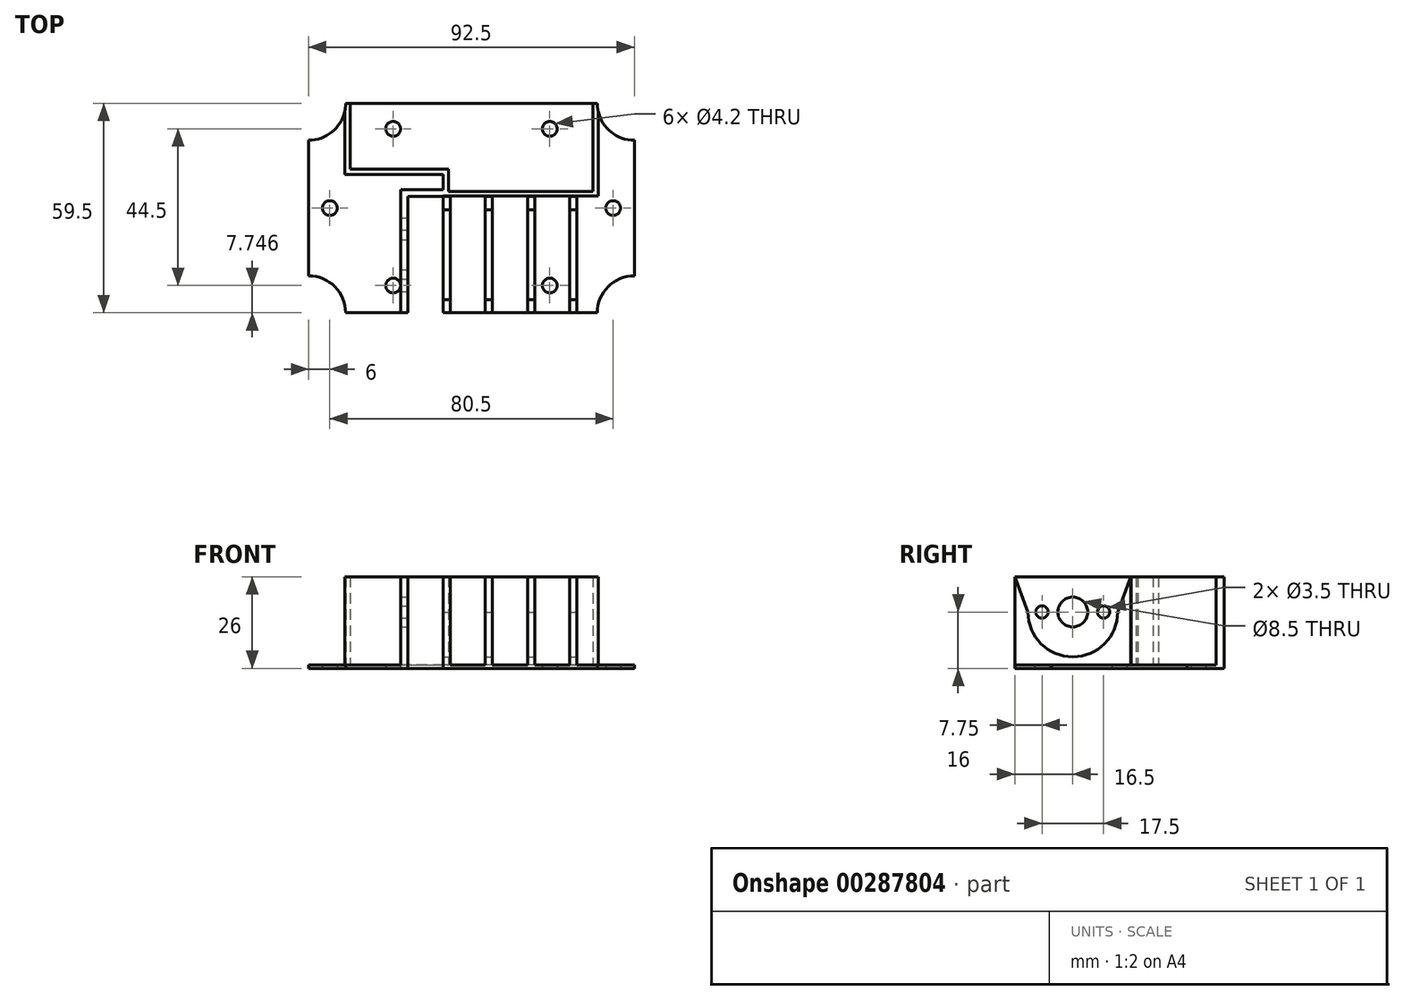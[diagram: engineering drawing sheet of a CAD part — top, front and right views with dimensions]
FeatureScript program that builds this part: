
annotation { "Feature Type Name" : "Feature", "Feature Type Description" : "" }
export const myFeature = defineFeature(function(context is Context, id is Id, definition is map)
    precondition{}
    {
        {
            var Q0;
            Q0=qCreatedBy(makeId("Top.planeOp"),FACE);
            var sketch = newSketch(context, id + "F0", { "sketchPlane" : qUnion([Q0])});
            skLineSegment(sketch, "E0", {"start": v(-40.25, 0) * mm, "end": v(40.25, 0) * mm, "construction": true});
            skLineSegment(sketch, "E1", {"start": v(22.25, 22.5) * mm, "end": v(22.25, -22) * mm, "construction": true});
            skPoint(sketch, "E2", {"position": v(0, 0) * mm});
            skLineSegment(sketch, "E3", {"start": v(22.25, 22.5) * mm, "end": v(-22.25, 22.5) * mm, "construction": true});
            skLineSegment(sketch, "E4", {"start": v(-22.25, 22.5) * mm, "end": v(-22.25, -22) * mm, "construction": true});
            skLineSegment(sketch, "E5", {"start": v(-22.25, -22) * mm, "end": v(22.25, -22) * mm, "construction": true});
            skLineSegment(sketch, "E6", {"start": v(0, 22.5) * mm, "end": v(0, -22) * mm, "construction": true});
            skCircle(sketch, "E7", {"center": v(-22.25, 22.5) * mm, "radius": 2.1 * mm});
            skCircle(sketch, "E8", {"center": v(22.25, 22.5) * mm, "radius": 2.1 * mm});
            skCircle(sketch, "E9", {"center": v(22.25, -22) * mm, "radius": 2.1 * mm});
            skCircle(sketch, "E10", {"center": v(-22.25, -22) * mm, "radius": 2.1 * mm});
            skCircle(sketch, "E11", {"center": v(-40.25, 0) * mm, "radius": 2.1 * mm});
            skCircle(sketch, "E12", {"center": v(40.25, 0) * mm, "radius": 2.1 * mm});
            skLineSegment(sketch, "E13.bottom", {"start": v(46.25, 29.75) * mm, "end": v(-46.25, 29.75) * mm});
            skLineSegment(sketch, "E13.top", {"start": v(46.25, -29.75) * mm, "end": v(-46.25, -29.75) * mm});
            skLineSegment(sketch, "E13.left", {"start": v(46.25, 29.75) * mm, "end": v(46.25, -29.75) * mm});
            skLineSegment(sketch, "E13.right", {"start": v(-46.25, 29.75) * mm, "end": v(-46.25, -29.75) * mm});
            skCircle(sketch, "E14", {"center": v(-46.25, 29.75) * mm, "radius": 10.5 * mm});
            skCircle(sketch, "E15.MirrorC", {"center": v(46.25, 29.75) * mm, "radius": 10.5 * mm});
            skCircle(sketch, "E16.MirrorC", {"center": v(-46.25, -29.75) * mm, "radius": 10.5 * mm});
            skCircle(sketch, "E17.MirrorC", {"center": v(46.25, -29.75) * mm, "radius": 10.5 * mm});
            skSolve(sketch);
        }
        {
            var Q0;
            Q0=makeQuery(id+"F0.imprint","IMPRINT",FACE,{"disambiguationData":[TD([[makeQuery(id+"F0.imprint","IMPRINT",EDGE,{"derivedFrom":sQuery(id+"F0.wireOp",EDGE,"E7")}),-1.0]])]});
            extrude(context, id + "F1", {"entities" : qUnion([Q0]), "depth" : 1 * mm});
        }
        {
            var Q0;
            Q0=makeQuery(id+"F1.opExtrude","CAP_FACE",FACE,{"disambiguationData":[OSD([sQuery(id+"F0.wireOp",EDGE,"E7"),sQuery(id+"F0.wireOp",EDGE,"E8"),sQuery(id+"F0.wireOp",EDGE,"E9"),sQuery(id+"F0.wireOp",EDGE,"E10"),sQuery(id+"F0.wireOp",EDGE,"E11"),sQuery(id+"F0.wireOp",EDGE,"E12"),sQuery(id+"F0.wireOp",EDGE,"E13.bottom"),sQuery(id+"F0.wireOp",EDGE,"E13.top"),sQuery(id+"F0.wireOp",EDGE,"E13.left"),sQuery(id+"F0.wireOp",EDGE,"E13.right"),sQuery(id+"F0.wireOp",EDGE,"E14"),sQuery(id+"F0.wireOp",EDGE,"E15.MirrorC"),sQuery(id+"F0.wireOp",EDGE,"E16.MirrorC"),sQuery(id+"F0.wireOp",EDGE,"E17.MirrorC")])],"isStart":false});
            var sketch = newSketch(context, id + "F2", { "sketchPlane" : qUnion([Q0])});
            skLineSegment(sketch, "E18.bottom", {"start": v(-34.5, 29.75) * mm, "end": v(34.5, 29.75) * mm});
            skLineSegment(sketch, "E18.top", {"start": v(-34.5, 11.08) * mm, "end": v(-6.5, 11.08) * mm});
            skLineSegment(sketch, "E18.left", {"start": v(-34.5, 29.75) * mm, "end": v(-34.5, 11.08) * mm});
            skLineSegment(sketch, "E18.right", {"start": v(34.5, 29.75) * mm, "end": v(34.5, 11.08) * mm});
            skLineSegment(sketch, "E19.bottom", {"start": v(-36, 29.75) * mm, "end": v(36, 29.75) * mm});
            skLineSegment(sketch, "E19.top", {"start": v(-36, 9.58) * mm, "end": v(-6.5, 9.58) * mm});
            skLineSegment(sketch, "E19.left", {"start": v(-36, 29.75) * mm, "end": v(-36, 9.58) * mm});
            skLineSegment(sketch, "E19.right", {"start": v(36, 29.75) * mm, "end": v(36, 9.58) * mm});
            skLineSegment(sketch, "E20", {"start": v(0, 29.75) * mm, "end": v(0, -29.75) * mm, "construction": true});
            skPoint(sketch, "E21", {"position": v(0, 11.08) * mm});
            skLineSegment(sketch, "E22.bottom", {"start": v(36, 9.58) * mm, "end": v(34.5, 9.58) * mm});
            skLineSegment(sketch, "E22.top", {"start": v(36, 3.4) * mm, "end": v(-8, 3.4) * mm});
            skLineSegment(sketch, "E22.left", {"start": v(36, 9.58) * mm, "end": v(36, 3.4) * mm});
            skLineSegment(sketch, "E22.right", {"start": v(-8, 9.58) * mm, "end": v(-8, 3.4) * mm});
            skLineSegment(sketch, "E23.top", {"start": v(34.5, 4.73) * mm, "end": v(-6.5, 4.73) * mm});
            skLineSegment(sketch, "E23.left", {"start": v(34.5, 9.58) * mm, "end": v(34.5, 4.73) * mm});
            skLineSegment(sketch, "E23.right", {"start": v(-6.5, 9.58) * mm, "end": v(-6.5, 4.73) * mm});
            skLineSegment(sketch, "E24", {"start": v(-6.5, 9.58) * mm, "end": v(-6.5, 11.08) * mm});
            skLineSegment(sketch, "E25", {"start": v(34.5, 11.08) * mm, "end": v(34.5, 9.58) * mm});
            skLineSegment(sketch, "E26.trimOffspring", {"start": v(34.5, 9.58) * mm, "end": v(36, 9.58) * mm});
            skLineSegment(sketch, "E27.trimOffspring", {"start": v(-6.5, 9.58) * mm, "end": v(-8, 9.58) * mm});
            skSolve(sketch);
        }
        {
            var Q0;
            Q0=makeQuery(id+"F2.imprint","IMPRINT",FACE,{"disambiguationData":[TD([[makeQuery(id+"F2.imprint","IMPRINT",EDGE,{"derivedFrom":sQuery(id+"F2.wireOp",EDGE,"E18.top")}),-1.0]])]});
            var Q1;
            Q1=makeQuery(id+"F2.imprint","IMPRINT",FACE,{"disambiguationData":[TD([[makeQuery(id+"F2.imprint","IMPRINT",EDGE,{"derivedFrom":sQuery(id+"F2.wireOp",EDGE,"E22.top")}),-1.0]])]});
            var Q2;
            {var subQ2=sQuery(id+"F2.wireOp",EDGE,"E18.right");Q2=makeQuery(id+"F2.imprint","IMPRINT",FACE,{"disambiguationData":[TD([[makeQuery(id+"F2.imprint","IMPRINT",EDGE,{"derivedFrom":subQ2}),1.0]])]});}
            extrude(context, id + "F3", {"entities" : qUnion([Q0, Q1, Q2]), "operationType" : NewBodyOperationType.ADD, "depth" : 25 * mm});
        }
        {
            var Q0;
            {var subQ0=sQuery(id+"F0.wireOp",EDGE,"E15.MirrorC");var subQ2=sQuery(id+"F0.wireOp",EDGE,"E14");var subQ4=sQuery(id+"F0.wireOp",EDGE,"E13.right");var subQ5=sQuery(id+"F0.wireOp",EDGE,"E13.left");var subQ7=sQuery(id+"F0.wireOp",EDGE,"E13.top");var subQ8=sQuery(id+"F0.wireOp",EDGE,"E13.bottom");var subQ9=sQuery(id+"F0.wireOp",EDGE,"E9");var subQ10=sQuery(id+"F0.wireOp",EDGE,"E10");var subQ11=sQuery(id+"F0.wireOp",EDGE,"E11");var subQ12=sQuery(id+"F0.wireOp",EDGE,"E12");var subQ13=sQuery(id+"F0.wireOp",EDGE,"E16.MirrorC");var subQ14=sQuery(id+"F0.wireOp",EDGE,"E17.MirrorC");Q0=makeQuery(id+"F3.boolean.opBoolean","SPLIT",FACE,{"disambiguationData":[TD([makeQuery(id+"F1.opExtrude","SWEPT_FACE",FACE,{"disambiguationData":[OSD([subQ9])]})])],"derivedFrom":makeQuery(id+"F1.opExtrude","CAP_FACE",FACE,{"disambiguationData":[OSD([sQuery(id+"F0.wireOp",EDGE,"E7"),sQuery(id+"F0.wireOp",EDGE,"E8"),subQ9,subQ10,subQ11,subQ12,subQ8,subQ7,subQ5,subQ4,subQ2,subQ0,subQ13,subQ14])],"isStart":false})});}
            var sketch = newSketch(context, id + "F4", { "sketchPlane" : qUnion([Q0])});
            skLineSegment(sketch, "E28.bottom", {"start": v(-18.06, -29.75) * mm, "end": v(-8.06, -29.75) * mm});
            skLineSegment(sketch, "E28.top", {"start": v(-18.06, 3.25) * mm, "end": v(-8.06, 3.25) * mm});
            skLineSegment(sketch, "E28.left", {"start": v(-18.06, -29.75) * mm, "end": v(-18.06, 3.25) * mm});
            skLineSegment(sketch, "E28.right", {"start": v(-8.06, -29.75) * mm, "end": v(-8.06, 3.25) * mm});
            skSolve(sketch);
        }
        {
            var Q0;
            {var subQ3=sQuery(id+"F4.wireOp",EDGE,"E28.bottom");Q0=makeQuery(id+"F4.imprint","IMPRINT",FACE,{"disambiguationData":[TD([[makeQuery(id+"F4.imprint","IMPRINT",EDGE,{"derivedFrom":subQ3}),-1.0]])]});}
            extrude(context, id + "F5", {"entities" : qUnion([Q0]), "operationType" : NewBodyOperationType.REMOVE, "oppositeDirection" : true, "depth" : 25 * mm});
        }
        {
            var Q0;
            {var subQ0=sQuery(id+"F0.wireOp",EDGE,"E15.MirrorC");var subQ2=sQuery(id+"F0.wireOp",EDGE,"E14");var subQ4=sQuery(id+"F0.wireOp",EDGE,"E13.right");var subQ5=sQuery(id+"F0.wireOp",EDGE,"E13.left");var subQ7=sQuery(id+"F0.wireOp",EDGE,"E13.bottom");var subQ9=sQuery(id+"F0.wireOp",EDGE,"E13.top");var subQ10=sQuery(id+"F0.wireOp",EDGE,"E9");var subQ11=sQuery(id+"F0.wireOp",EDGE,"E10");var subQ12=sQuery(id+"F0.wireOp",EDGE,"E11");var subQ13=sQuery(id+"F0.wireOp",EDGE,"E12");var subQ14=sQuery(id+"F0.wireOp",EDGE,"E16.MirrorC");var subQ15=sQuery(id+"F0.wireOp",EDGE,"E17.MirrorC");Q0=makeQuery(id+"F3.boolean.opBoolean","SPLIT",FACE,{"disambiguationData":[TD([makeQuery(id+"F1.opExtrude","SWEPT_FACE",FACE,{"disambiguationData":[OSD([subQ10])]})])],"derivedFrom":makeQuery(id+"F1.opExtrude","CAP_FACE",FACE,{"disambiguationData":[OSD([sQuery(id+"F0.wireOp",EDGE,"E7"),sQuery(id+"F0.wireOp",EDGE,"E8"),subQ10,subQ11,subQ12,subQ13,subQ7,subQ9,subQ5,subQ4,subQ2,subQ0,subQ14,subQ15])],"isStart":false})});}
            var sketch = newSketch(context, id + "F6", { "sketchPlane" : qUnion([Q0])});
            skLineSegment(sketch, "E29.bottom", {"start": v(-8.06, 3.25) * mm, "end": v(-6.06, 3.25) * mm});
            skLineSegment(sketch, "E29.top", {"start": v(-8.06, -29.75) * mm, "end": v(-6.06, -29.75) * mm});
            skLineSegment(sketch, "E29.left", {"start": v(-8.06, 3.25) * mm, "end": v(-8.06, -29.75) * mm});
            skLineSegment(sketch, "E29.right", {"start": v(-6.06, 3.25) * mm, "end": v(-6.06, -29.75) * mm});
            skLineSegment(sketch, "E30.bottom", {"start": v(-18.06, 3.25) * mm, "end": v(-8, 3.25) * mm});
            skLineSegment(sketch, "E30.top", {"start": v(-18.06, 5.25) * mm, "end": v(-8, 5.25) * mm});
            skLineSegment(sketch, "E30.left", {"start": v(-18.06, 3.25) * mm, "end": v(-18.06, 5.25) * mm});
            skLineSegment(sketch, "E30.right", {"start": v(-8, 3.25) * mm, "end": v(-8, 5.25) * mm});
            skLineSegment(sketch, "E31.bottom", {"start": v(-18.06, -29.75) * mm, "end": v(-20.06, -29.75) * mm});
            skLineSegment(sketch, "E31.top", {"start": v(-18.06, 5.25) * mm, "end": v(-20.06, 5.25) * mm});
            skLineSegment(sketch, "E31.left", {"start": v(-18.06, -29.75) * mm, "end": v(-18.06, 5.25) * mm});
            skLineSegment(sketch, "E31.right", {"start": v(-20.06, -29.75) * mm, "end": v(-20.06, -25) * mm});
            skLineSegment(sketch, "E32.trimOffspring", {"start": v(-20.06, -19.02) * mm, "end": v(-20.06, 5.25) * mm});
            skLineSegment(sketch, "E33.1.0.0", {"start": v(5.94, 3.25) * mm, "end": v(5.94, -29.75) * mm});
            skLineSegment(sketch, "E33.1.0.1", {"start": v(3.94, 3.25) * mm, "end": v(3.94, -29.75) * mm});
            skLineSegment(sketch, "E33.1.0.2", {"start": v(3.94, -29.75) * mm, "end": v(5.94, -29.75) * mm});
            skLineSegment(sketch, "E33.1.0.3", {"start": v(3.94, 3.25) * mm, "end": v(5.94, 3.25) * mm});
            skLineSegment(sketch, "E33.2.0.0", {"start": v(17.94, 3.25) * mm, "end": v(17.94, -29.75) * mm});
            skLineSegment(sketch, "E33.2.0.1", {"start": v(15.94, 3.25) * mm, "end": v(15.94, -29.75) * mm});
            skLineSegment(sketch, "E33.2.0.2", {"start": v(15.94, -29.75) * mm, "end": v(17.94, -29.75) * mm});
            skLineSegment(sketch, "E33.2.0.3", {"start": v(15.94, 3.25) * mm, "end": v(17.94, 3.25) * mm});
            skLineSegment(sketch, "E33.3.0.0", {"start": v(29.94, 3.25) * mm, "end": v(29.94, -29.75) * mm});
            skLineSegment(sketch, "E33.3.0.1", {"start": v(27.94, 3.25) * mm, "end": v(27.94, -29.75) * mm});
            skLineSegment(sketch, "E33.3.0.2", {"start": v(27.94, -29.75) * mm, "end": v(29.94, -29.75) * mm});
            skLineSegment(sketch, "E33.3.0.3", {"start": v(27.94, 3.25) * mm, "end": v(29.94, 3.25) * mm});
            skLineSegment(sketch, "E33.direction1", {"start": v(-6.06, -29.75) * mm, "end": v(5.94, -29.75) * mm, "construction": true});
            skLineSegment(sketch, "E34", {"start": v(-20.06, -19.02) * mm, "end": v(-20.06, -25) * mm});
            skPoint(sketch, "E35.center.orphan", {"position": v(-22.25, -22) * mm});
            skSolve(sketch);
        }
        {
            var Q0;
            {var subQ3=sQuery(id+"F6.wireOp",EDGE,"E31.bottom");Q0=makeQuery(id+"F6.imprint","IMPRINT",FACE,{"disambiguationData":[TD([[makeQuery(id+"F6.imprint","IMPRINT",EDGE,{"derivedFrom":subQ3}),-1.0]])]});}
            var Q1;
            {var subQ3=sQuery(id+"F6.wireOp",EDGE,"E30.bottom");Q1=makeQuery(id+"F6.imprint","IMPRINT",FACE,{"disambiguationData":[TD([[makeQuery(id+"F6.imprint","IMPRINT",EDGE,{"derivedFrom":subQ3}),1.0]])]});}
            var Q2;
            Q2=makeQuery(id+"F6.imprint","IMPRINT",FACE,{"disambiguationData":[TD([[makeQuery(id+"F6.imprint","IMPRINT",EDGE,{"derivedFrom":sQuery(id+"F6.wireOp",EDGE,"E29.bottom")}),-1.0]])]});
            var Q3;
            Q3=makeQuery(id+"F6.imprint","IMPRINT",FACE,{"disambiguationData":[TD([[makeQuery(id+"F6.imprint","IMPRINT",EDGE,{"derivedFrom":sQuery(id+"F6.wireOp",EDGE,"E33.1.0.0")}),-1.0]])]});
            var Q4;
            Q4=makeQuery(id+"F6.imprint","IMPRINT",FACE,{"disambiguationData":[TD([[makeQuery(id+"F6.imprint","IMPRINT",EDGE,{"derivedFrom":sQuery(id+"F6.wireOp",EDGE,"E33.2.0.0")}),-1.0]])]});
            var Q5;
            Q5=makeQuery(id+"F6.imprint","IMPRINT",FACE,{"disambiguationData":[TD([[makeQuery(id+"F6.imprint","IMPRINT",EDGE,{"derivedFrom":sQuery(id+"F6.wireOp",EDGE,"E33.3.0.0")}),-1.0]])]});
            extrude(context, id + "F7", {"entities" : qUnion([Q0, Q1, Q2, Q3, Q4, Q5]), "operationType" : NewBodyOperationType.ADD, "depth" : 25 * mm});
        }
        {
            var Q0;
            Q0=makeQuery(id+"F7.opExtrude","SWEPT_FACE",FACE,{"disambiguationData":[OSD([sQuery(id+"F6.wireOp",EDGE,"E33.3.0.0")])]});
            var sketch = newSketch(context, id + "F8", { "sketchPlane" : qUnion([Q0])});
            skCircle(sketch, "E36", {"center": v(-13.25, 16) * mm, "radius": 12.75 * mm});
            skLineSegment(sketch, "E37", {"start": v(-29.75, 26) * mm, "end": v(3.25, 1) * mm, "construction": true});
            skLineSegment(sketch, "E38", {"start": v(3.25, 26) * mm, "end": v(-29.75, 1) * mm, "construction": true});
            skPoint(sketch, "E39", {"position": v(-13.25, 13.5) * mm});
            skLineSegment(sketch, "E40", {"start": v(-13.25, 13.5) * mm, "end": v(-13.25, 16.14) * mm, "construction": true});
            skLineSegment(sketch, "E41", {"start": v(-29.75, 16) * mm, "end": v(3.25, 16) * mm, "construction": true});
            skLineSegment(sketch, "E42", {"start": v(-26, 16) * mm, "end": v(-29.75, 26) * mm});
            skLineSegment(sketch, "E43", {"start": v(-13.25, 1) * mm, "end": v(-13.25, 26) * mm, "construction": true});
            skLineSegment(sketch, "E44.MirrorCS", {"start": v(-0.5, 16) * mm, "end": v(3.25, 26) * mm});
            skSolve(sketch);
        }
        {
            var Q0;
            {var subQ0=sQuery(id+"F8.wireOp",EDGE,"E36");var subQ1=sQuery(id+"F6.wireOp",EDGE,"E33.3.0.0");var subQ2=makeQuery(id+"F7.opExtrude","CAP_EDGE",EDGE,{"disambiguationData":[OSD([subQ1])],"isStart":false});var subQ3=makeQuery(id+"F8.imprint","INTERSECT",VERTEX,{"disambiguationData":[OD(0.0)],"derivedFrom":[subQ2,subQ0]});Q0=makeQuery(id+"F8.imprint","IMPRINT",FACE,{"disambiguationData":[TD([[makeQuery(id+"F8.imprint","IMPRINT",EDGE,{"disambiguationData":[TD([[subQ3,-1.0]])],"derivedFrom":subQ0}),1.0]])]});}
            var Q1;
            {var subQ1=sQuery(id+"F8.wireOp",EDGE,"E36");var subQ8=sQuery(id+"F8.wireOp",EDGE,"E44.MirrorCS");var subQ11=makeQuery(id+"F8.imprint","INTERSECT",VERTEX,{"disambiguationData":[OD(1.0)],"derivedFrom":[subQ1,subQ8]});Q1=makeQuery(id+"F8.imprint","IMPRINT",FACE,{"disambiguationData":[TD([[makeQuery(id+"F8.imprint","IMPRINT",EDGE,{"disambiguationData":[TD([[subQ11,-1.0]])],"derivedFrom":subQ1}),1.0]])]});}
            var Q2;
            {var subQ0=sQuery(id+"F8.wireOp",EDGE,"E42");var subQ1=sQuery(id+"F8.wireOp",EDGE,"E36");var subQ2=makeQuery(id+"F8.imprint","INTERSECT",VERTEX,{"disambiguationData":[OD(1.0)],"derivedFrom":[subQ1,subQ0]});Q2=makeQuery(id+"F8.imprint","IMPRINT",FACE,{"disambiguationData":[TD([[makeQuery(id+"F8.imprint","IMPRINT",EDGE,{"disambiguationData":[TD([[subQ2,1.0]])],"derivedFrom":subQ1}),-1.0]])]});}
            var Q3;
            {var subQ0=sQuery(id+"F8.wireOp",EDGE,"E44.MirrorCS");var subQ1=sQuery(id+"F8.wireOp",EDGE,"E36");var subQ2=makeQuery(id+"F8.imprint","INTERSECT",VERTEX,{"disambiguationData":[OD(1.0)],"derivedFrom":[subQ1,subQ0]});Q3=makeQuery(id+"F8.imprint","IMPRINT",FACE,{"disambiguationData":[TD([[makeQuery(id+"F8.imprint","IMPRINT",EDGE,{"disambiguationData":[TD([[subQ2,-1.0]])],"derivedFrom":subQ1}),-1.0]])]});}
            var Q4;
            Q4=makeQuery(id+"F7.boolean.opBoolean","MERGE",FACE,{"derivedFrom":[makeQuery(id+"F5.boolean.opBoolean","COPY",FACE,{"derivedFrom":makeQuery(id+"F5.opExtrude","SWEPT_FACE",FACE,{"disambiguationData":[OSD([sQuery(id+"F4.wireOp",EDGE,"E28.right")])]})}),makeQuery(id+"F7.opExtrude","SWEPT_FACE",FACE,{"disambiguationData":[OSD([sQuery(id+"F6.wireOp",EDGE,"E29.left")])]})]});
            extrude(context, id + "F9", {"entities" : qUnion([Q0, Q1, Q2, Q3]), "operationType" : NewBodyOperationType.REMOVE, "endBound" : BoundingType.UP_TO_SURFACE, "oppositeDirection" : true, "endBoundEntityFace" : qUnion([Q4]), "depth" : 25 * mm});
        }
        {
            var Q0;
            Q0=makeQuery(id+"F7.boolean.opBoolean","MERGE",FACE,{"derivedFrom":[makeQuery(id+"F5.boolean.opBoolean","COPY",FACE,{"derivedFrom":makeQuery(id+"F5.opExtrude","SWEPT_FACE",FACE,{"disambiguationData":[OSD([sQuery(id+"F4.wireOp",EDGE,"E28.left")])]})}),makeQuery(id+"F7.opExtrude","SWEPT_FACE",FACE,{"disambiguationData":[OSD([sQuery(id+"F6.wireOp",EDGE,"E31.left")])]})]});
            var sketch = newSketch(context, id + "F10", { "sketchPlane" : qUnion([Q0])});
            skLineSegment(sketch, "E45", {"start": v(-29.75, 26) * mm, "end": v(3.25, 1.21) * mm, "construction": true});
            skLineSegment(sketch, "E46", {"start": v(3.25, 26) * mm, "end": v(-29.75, 1.12) * mm, "construction": true});
            skPoint(sketch, "E47", {"position": v(-13.25, 13.6) * mm});
            skLineSegment(sketch, "E48", {"start": v(-13.25, 13.6) * mm, "end": v(-13.25, 20.71) * mm, "construction": true});
            skCircle(sketch, "E49", {"center": v(-13.25, 16) * mm, "radius": 12.75 * mm});
            skLineSegment(sketch, "E50", {"start": v(-22, 16) * mm, "end": v(-4.5, 16) * mm, "construction": true});
            skCircle(sketch, "E51", {"center": v(-22, 16) * mm, "radius": 1.75 * mm});
            skCircle(sketch, "E52", {"center": v(-4.5, 16) * mm, "radius": 1.75 * mm});
            skCircle(sketch, "E53", {"center": v(-13.25, 16) * mm, "radius": 4.25 * mm});
            skSolve(sketch);
        }
        {
            var Q0;
            Q0=makeQuery(id+"F10.imprint","IMPRINT",FACE,{"disambiguationData":[TD([[makeQuery(id+"F10.imprint","IMPRINT",EDGE,{"derivedFrom":sQuery(id+"F10.wireOp",EDGE,"E53")}),1.0]])]});
            var Q1;
            Q1=makeQuery(id+"F10.imprint","IMPRINT",FACE,{"disambiguationData":[TD([[makeQuery(id+"F10.imprint","IMPRINT",EDGE,{"derivedFrom":sQuery(id+"F10.wireOp",EDGE,"E52")}),1.0]])]});
            var Q2;
            Q2=makeQuery(id+"F10.imprint","IMPRINT",FACE,{"disambiguationData":[TD([[makeQuery(id+"F10.imprint","IMPRINT",EDGE,{"derivedFrom":sQuery(id+"F10.wireOp",EDGE,"E51")}),1.0]])]});
            extrude(context, id + "F11", {"entities" : qUnion([Q0, Q1, Q2]), "operationType" : NewBodyOperationType.REMOVE, "oppositeDirection" : true, "depth" : 25 * mm});
        }
    });
